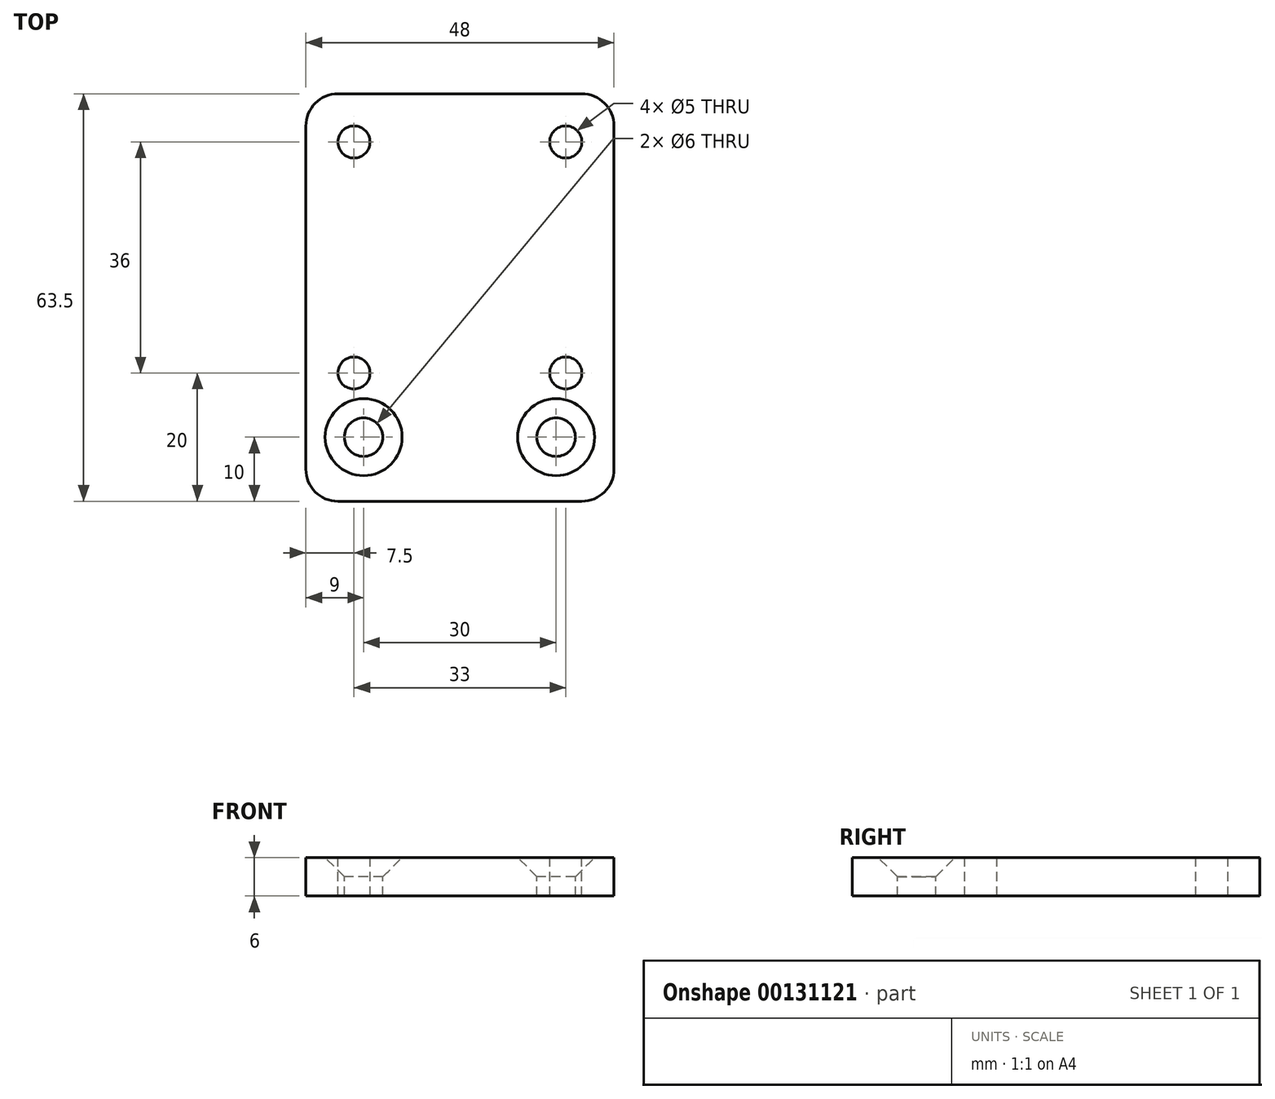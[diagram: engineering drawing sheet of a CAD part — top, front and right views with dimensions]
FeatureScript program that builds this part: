
annotation { "Feature Type Name" : "Feature", "Feature Type Description" : "" }
export const myFeature = defineFeature(function(context is Context, id is Id, definition is map)
    precondition{}
    {
        {
            var Q0;
            Q0=qCreatedBy(makeId("Top.planeOp"),FACE);
            var sketch = newSketch(context, id + "F0", { "sketchPlane" : qUnion([Q0])});
            skLineSegment(sketch, "E0.bottom", {"start": v(24, -19) * mm, "end": v(-24, -19) * mm});
            skLineSegment(sketch, "E0.top", {"start": v(24, 44.5) * mm, "end": v(-24, 44.5) * mm});
            skLineSegment(sketch, "E0.right", {"start": v(-24, -19) * mm, "end": v(-24, 44.5) * mm});
            skPoint(sketch, "E1", {"position": v(16.5, 37) * mm});
            skPoint(sketch, "E2", {"position": v(16.5, 1) * mm});
            skPoint(sketch, "E3", {"position": v(-16.5, 37) * mm});
            skPoint(sketch, "E4", {"position": v(-16.5, 1) * mm});
            skPoint(sketch, "E5", {"position": v(15, -9) * mm});
            skPoint(sketch, "E6", {"position": v(-15, -9) * mm});
            skLineSegment(sketch, "E7", {"start": v(24, 44.5) * mm, "end": v(24, -19) * mm});
            skSolve(sketch);
        }
        {
            var Q0;
            Q0=makeQuery(id+"F0.imprint","IMPRINT",FACE,{"disambiguationData":[TD([[makeQuery(id+"F0.imprint","IMPRINT",EDGE,{"derivedFrom":sQuery(id+"F0.wireOp",EDGE,"E0.bottom")}),-1.0]])]});
            extrude(context, id + "F1", {"entities" : qUnion([Q0]), "oppositeDirection" : true, "depth" : 6 * mm});
        }
        {
            var Q0;
            Q0=makeQuery(id+"F1.opExtrude","SWEPT_EDGE",EDGE,{"disambiguationData":[OSD([sQuery(id+"F0.wireOp",EDGE,"E0.bottom"),sQuery(id+"F0.wireOp",EDGE,"E0.right")])]});
            var Q1;
            Q1=makeQuery(id+"F1.opExtrude","SWEPT_EDGE",EDGE,{"disambiguationData":[OSD([sQuery(id+"F0.wireOp",EDGE,"E0.bottom"),sQuery(id+"F0.wireOp",EDGE,"E0.left")])]});
            var Q2;
            Q2=makeQuery(id+"F1.opExtrude","SWEPT_EDGE",EDGE,{"disambiguationData":[OSD([sQuery(id+"F0.wireOp",EDGE,"lGIGnHYG-dv0g-Brav-alXV-JeUitXMt4tIn.bottom"),sQuery(id+"F0.wireOp",EDGE,"lGIGnHYG-dv0g-Brav-alXV-JeUitXMt4tIn.left")])]});
            var Q3;
            Q3=makeQuery(id+"F1.opExtrude","SWEPT_EDGE",EDGE,{"disambiguationData":[OSD([sQuery(id+"F0.wireOp",EDGE,"E0.left"),sQuery(id+"F0.wireOp",EDGE,"lGIGnHYG-dv0g-Brav-alXV-JeUitXMt4tIn.bottom")])]});
            var Q4;
            Q4=makeQuery(id+"F1.opExtrude","SWEPT_EDGE",EDGE,{"disambiguationData":[OSD([sQuery(id+"F0.wireOp",EDGE,"lGIGnHYG-dv0g-Brav-alXV-JeUitXMt4tIn.top"),sQuery(id+"F0.wireOp",EDGE,"lGIGnHYG-dv0g-Brav-alXV-JeUitXMt4tIn.left")])]});
            var Q5;
            Q5=makeQuery(id+"F1.opExtrude","SWEPT_EDGE",EDGE,{"disambiguationData":[OSD([sQuery(id+"F0.wireOp",EDGE,"E0.top"),sQuery(id+"F0.wireOp",EDGE,"1V1XXEP0-sfIm-Kzud-gfrB-fWnKi3KGei4T")])]});
            var Q6;
            Q6=makeQuery(id+"F1.opExtrude","SWEPT_EDGE",EDGE,{"disambiguationData":[OSD([sQuery(id+"F0.wireOp",EDGE,"lGIGnHYG-dv0g-Brav-alXV-JeUitXMt4tIn.top"),sQuery(id+"F0.wireOp",EDGE,"1V1XXEP0-sfIm-Kzud-gfrB-fWnKi3KGei4T")])]});
            var Q7;
            Q7=makeQuery(id+"F1.opExtrude","SWEPT_EDGE",EDGE,{"disambiguationData":[OSD([sQuery(id+"F0.wireOp",EDGE,"E0.top"),sQuery(id+"F0.wireOp",EDGE,"E0.right")])]});
            fillet(context, id + "F2", {"entities" : qUnion([Q0, Q1, Q2, Q3, Q4, Q5, Q6, Q7]), "radius" : 5 * mm, "allowEdgeOverflow" : false});
        }
        {
            var Q0;
            Q0=sQuery(id+"F0.wireOp",VERTEX,"E2");
            var Q1;
            Q1=sQuery(id+"F0.wireOp",VERTEX,"E4");
            var Q2;
            Q2=sQuery(id+"F0.wireOp",VERTEX,"E1");
            var Q3;
            Q3=sQuery(id+"F0.wireOp",VERTEX,"E3");
            var Q4;
            Q4=makeQuery(id+"F1.opExtrude","SWEPT_BODY",BODY,{"disambiguationData":[OSD([sQuery(id+"F0.wireOp",EDGE,"E0.bottom"),sQuery(id+"F0.wireOp",EDGE,"E0.top"),sQuery(id+"F0.wireOp",EDGE,"E0.left"),sQuery(id+"F0.wireOp",EDGE,"E0.right")])]});
            hole(context, id + "F3", {"style" : HoleStyle.SIMPLE, "endStyle" : HoleEndStyle.THROUGH, "holeDiameter" : 5 * mm, "locations" : qUnion([Q0, Q1, Q2, Q3]), "scope" : qUnion([Q4]), "isTappedThrough" : true});
        }
        {
            var Q0;
            Q0=sQuery(id+"F0.wireOp",VERTEX,"E5");
            var Q1;
            Q1=sQuery(id+"F0.wireOp",VERTEX,"E6");
            var Q2;
            Q2=makeQuery(id+"F1.opExtrude","SWEPT_BODY",BODY,{"disambiguationData":[OSD([sQuery(id+"F0.wireOp",EDGE,"E0.bottom"),sQuery(id+"F0.wireOp",EDGE,"E0.top"),sQuery(id+"F0.wireOp",EDGE,"E0.left"),sQuery(id+"F0.wireOp",EDGE,"E0.right")])]});
            hole(context, id + "F4", {"style" : HoleStyle.C_SINK, "endStyle" : HoleEndStyle.THROUGH, "holeDiameter" : 6 * mm, "cSinkDiameter" : 12 * mm, "cSinkAngle" : 90 * degree, "locations" : qUnion([Q0, Q1]), "scope" : qUnion([Q2]), "isTappedThrough" : true});
        }
    });
